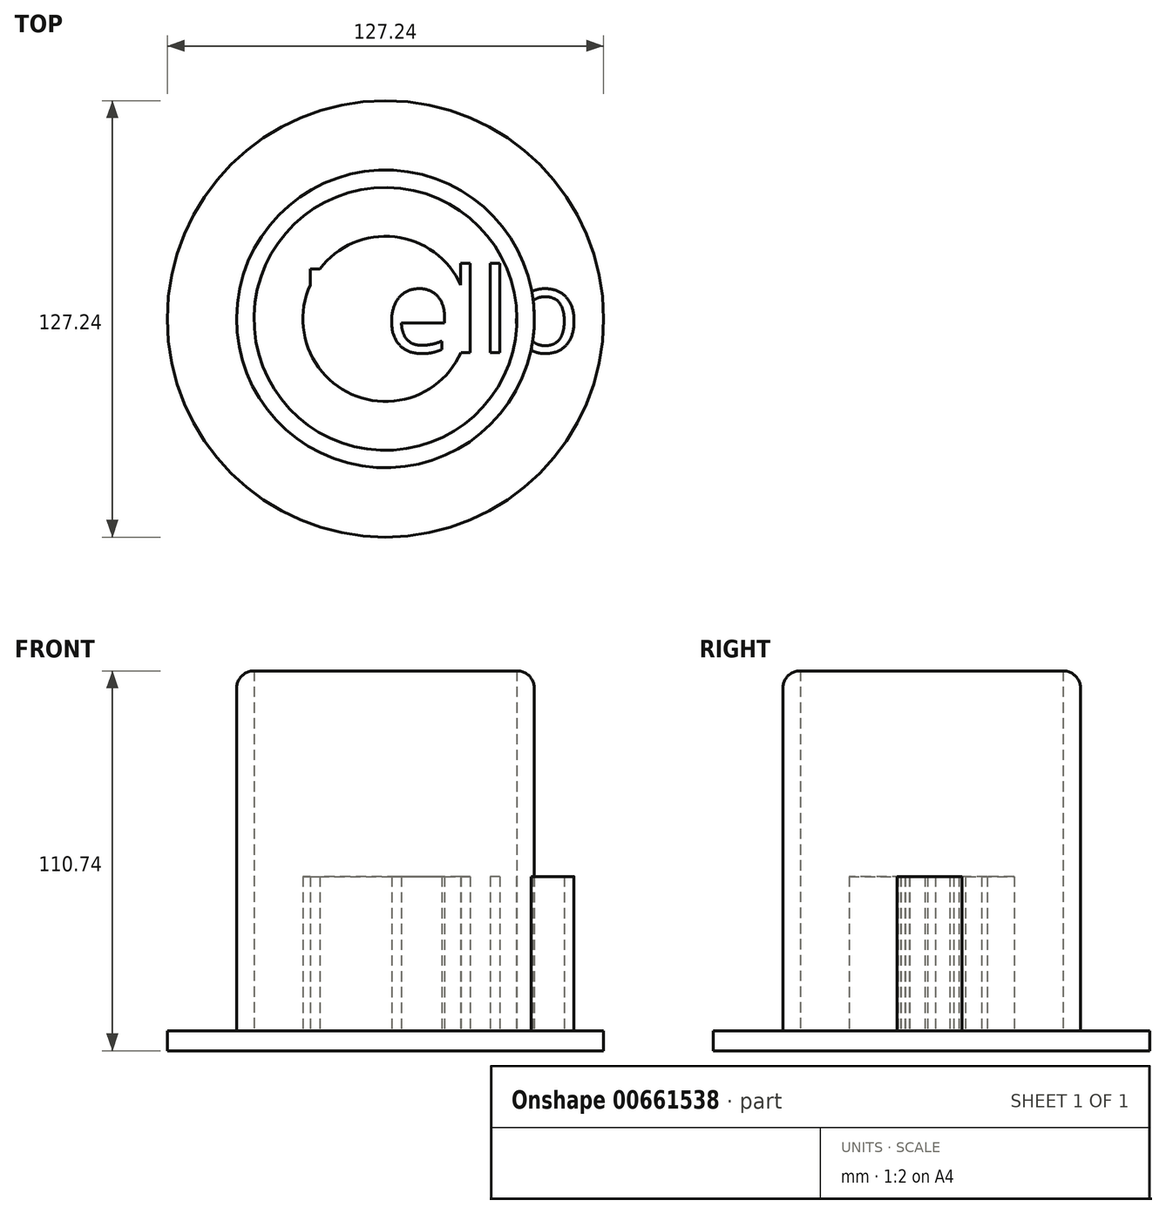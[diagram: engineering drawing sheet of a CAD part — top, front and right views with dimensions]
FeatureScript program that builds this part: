
annotation { "Feature Type Name" : "Feature", "Feature Type Description" : "" }
export const myFeature = defineFeature(function(context is Context, id is Id, definition is map)
    precondition{}
    {
        {
            var Q0;
            Q0=qCreatedBy(makeId("Top.planeOp"),FACE);
            var sketch = newSketch(context, id + "F0", { "sketchPlane" : qUnion([Q0])});
            skCircle(sketch, "E0", {"center": v(0, 0) * mm, "radius": 43.4 * mm});
            skSolve(sketch);
        }
        {
            var Q0;
            Q0 = qSketchRegion(id + "F0", true);
            extrude(context, id + "F1", {"entities" : qUnion([Q0]), "depth" : 110.74 * mm, "offsetDistance" : 25.4 * mm});
        }
        {
            var Q0;
            Q0=makeQuery(id+"F1.opExtrude","CAP_FACE",FACE,{"disambiguationData":[OSD([sQuery(id+"F0.wireOp",EDGE,"E0")])],"isStart":false});
            shell(context, id + "F2", {"entities" : qUnion([Q0]), "thickness" : 5.08 * mm});
        }
        {
            var Q0;
            Q0=qCreatedBy(makeId("Top.planeOp"),FACE);
            var sketch = newSketch(context, id + "F3", { "sketchPlane" : qUnion([Q0])});
            skCircle(sketch, "E1", {"center": v(0, 0) * mm, "radius": 63.62 * mm});
            skSolve(sketch);
        }
        {
            var Q0;
            Q0=makeQuery(id+"F3.imprint","IMPRINT",FACE,{"disambiguationData":[TD([[makeQuery(id+"F3.imprint","IMPRINT",EDGE,{"derivedFrom":sQuery(id+"F3.wireOp",EDGE,"E1")}),1.0]])]});
            extrude(context, id + "F4", {"entities" : qUnion([Q0]), "operationType" : NewBodyOperationType.ADD, "depth" : 5.84 * mm, "offsetDistance" : 25.4 * mm});
        }
        {
            var Q0;
            Q0=makeQuery(id+"F1.opExtrude","CAP_EDGE",EDGE,{"disambiguationData":[OSD([sQuery(id+"F0.wireOp",EDGE,"E0")])],"isStart":false});
            fillet(context, id + "F5", {"entities" : qUnion([Q0]), "radius" : 5.08 * mm, "tangentPropagation" : true, "allowEdgeOverflow" : false});
        }
        {
            var Q0;
            Q0=qCreatedBy(makeId("Top.planeOp"),FACE);
            var sketch = newSketch(context, id + "F6", { "sketchPlane" : qUnion([Q0])});
            skCircle(sketch, "E2", {"center": v(0, 0) * mm, "radius": 24.08 * mm});
            skText(sketch, "E3", { "text": "Hello\n", "fontName": "OpenSans-Regular.ttf"});
            const initialGuessF6  = {"E3": [-0.0253, -0.00978, 1, 0, 0.02457]};
            skSetInitialGuess(sketch, initialGuessF6);
            skSolve(sketch);
        }
        {
            var Q0;
            Q0 = qSketchRegion(id + "F6", true);
            extrude(context, id + "F7", {"entities" : qUnion([Q0]), "operationType" : NewBodyOperationType.ADD, "depth" : 50.8 * mm, "offsetDistance" : 25.4 * mm});
        }
    });
